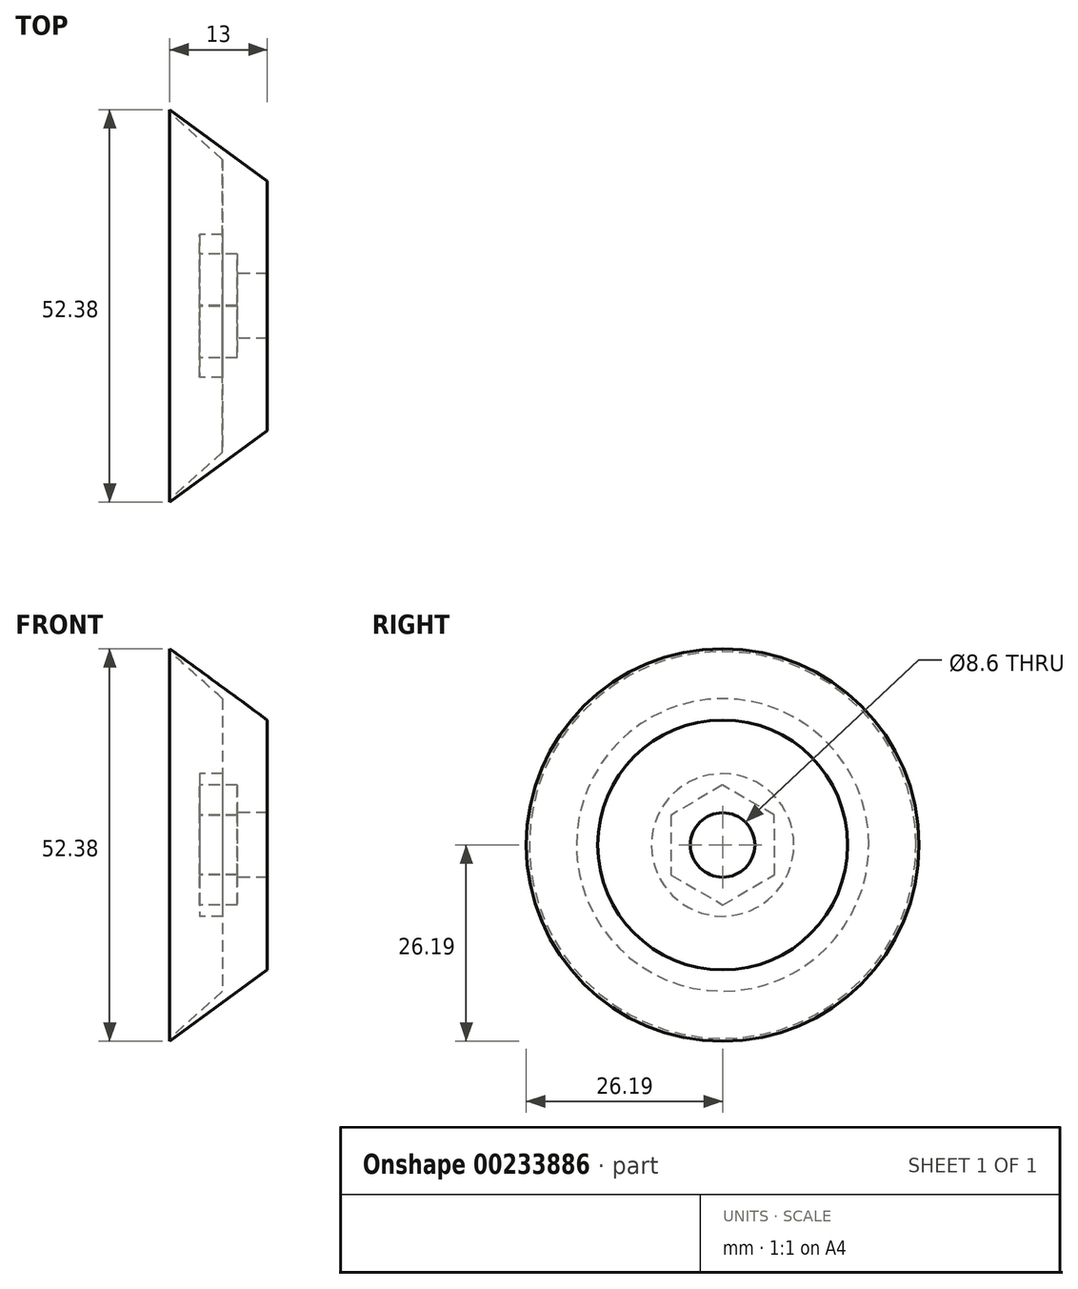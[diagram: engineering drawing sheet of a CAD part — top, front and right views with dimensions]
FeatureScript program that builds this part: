
annotation { "Feature Type Name" : "Feature", "Feature Type Description" : "" }
export const myFeature = defineFeature(function(context is Context, id is Id, definition is map)
    precondition{}
    {
        {
            var Q0;
            Q0=qCreatedBy(makeId("Front.planeOp"),FACE);
            var sketch = newSketch(context, id + "F0", { "sketchPlane" : qUnion([Q0])});
            skLineSegment(sketch, "E0", {"start": v(0, 72.01) * mm, "end": v(0, -72.04) * mm, "construction": true});
            skLineSegment(sketch, "E1", {"start": v(8, 67.17) * mm, "end": v(8, -65.75) * mm, "construction": true});
            skLineSegment(sketch, "E2", {"start": v(13, 61.84) * mm, "end": v(13, -59.21) * mm, "construction": true});
            skLineSegment(sketch, "E3", {"start": v(4, 59.18) * mm, "end": v(4, -52.92) * mm, "construction": true});
            skLineSegment(sketch, "E4", {"start": v(-49.7, 26.2) * mm, "end": v(61.22, 26.2) * mm, "construction": true});
            skLineSegment(sketch, "E5", {"start": v(-38.47, 14) * mm, "end": v(53.28, 14) * mm, "construction": true});
            skLineSegment(sketch, "E6", {"start": v(-32.84, 9.5) * mm, "end": v(36.11, 9.5) * mm, "construction": true});
            skLineSegment(sketch, "E7", {"start": v(-26.09, 4.3) * mm, "end": v(34.85, 4.3) * mm, "construction": true});
            skLineSegment(sketch, "E8", {"start": v(4, 4.3) * mm, "end": v(13, 4.3) * mm});
            skLineSegment(sketch, "E9", {"start": v(13, 4.3) * mm, "end": v(13, 9.5) * mm});
            skLineSegment(sketch, "E10", {"start": v(8, 14) * mm, "end": v(8, 19.5) * mm});
            skLineSegment(sketch, "E11", {"start": v(0, 26.2) * mm, "end": v(0, 25.79) * mm});
            skLineSegment(sketch, "E12", {"start": v(0, 25.79) * mm, "end": v(7.05, 19.5) * mm});
            skLineSegment(sketch, "E13", {"start": v(7.05, 19.5) * mm, "end": v(7.05, 9.5) * mm});
            skLineSegment(sketch, "E14", {"start": v(7.05, 9.5) * mm, "end": v(4, 9.5) * mm});
            skLineSegment(sketch, "E15", {"start": v(4, 9.5) * mm, "end": v(4, 4.3) * mm});
            skLineSegment(sketch, "E16", {"start": v(-60.7, 0) * mm, "end": v(65.05, 0) * mm, "construction": true});
            skLineSegment(sketch, "E17", {"start": v(0, 26.2) * mm, "end": v(13, 16.66) * mm});
            skLineSegment(sketch, "E18", {"start": v(13, 16.66) * mm, "end": v(13, 4.3) * mm});
            skSolve(sketch);
        }
        {
            var Q0;
            Q0=makeQuery(id+"F0.imprint","IMPRINT",FACE,{"disambiguationData":[TD([[makeQuery(id+"F0.imprint","IMPRINT",EDGE,{"derivedFrom":sQuery(id+"F0.wireOp",EDGE,"E8")}),1.0]])]});
            var Q1;
            Q1=sQuery(id+"F0.wireOp",EDGE,"E16");
            revolve(context, id + "F1", {"entities" : qUnion([Q0]), "axis" : qUnion([Q1]), "revolveType" : RevolveType.FULL});
        }
        {
            var Q0;
            Q0=makeQuery(id+"F1.opRevolve","SWEPT_FACE",FACE,{"disambiguationData":[OSD([sQuery(id+"F0.wireOp",EDGE,"E15")])]});
            var sketch = newSketch(context, id + "F2", { "sketchPlane" : qUnion([Q0])});
            skCircle(sketch, "E19.cCircle", {"center": v(0, 0) * mm, "radius": 6.91 * mm, "construction": true});
            skLineSegment(sketch, "E19.0", {"start": v(-6.9, 4.03) * mm, "end": v(0.04, 7.98) * mm});
            skLineSegment(sketch, "E19.1", {"start": v(0.04, 7.98) * mm, "end": v(6.93, 3.96) * mm});
            skLineSegment(sketch, "E19.2", {"start": v(6.93, 3.96) * mm, "end": v(6.9, -4.03) * mm});
            skLineSegment(sketch, "E19.3", {"start": v(6.9, -4.03) * mm, "end": v(-0.04, -7.98) * mm});
            skLineSegment(sketch, "E19.4", {"start": v(-0.04, -7.98) * mm, "end": v(-6.93, -3.96) * mm});
            skLineSegment(sketch, "E19.5", {"start": v(-6.93, -3.96) * mm, "end": v(-6.9, 4.03) * mm});
            skPoint(sketch, "E19.0.midPoint", {"position": v(-3.43, 6) * mm});
            skSolve(sketch);
        }
        {
            var Q0;
            Q0=makeQuery(id+"F2.imprint","IMPRINT",FACE,{"disambiguationData":[TD([[makeQuery(id+"F2.imprint","IMPRINT",EDGE,{"derivedFrom":sQuery(id+"F2.wireOp",EDGE,"E19.0")}),-1.0]])]});
            extrude(context, id + "F3", {"entities" : qUnion([Q0]), "operationType" : NewBodyOperationType.REMOVE, "oppositeDirection" : true, "depth" : 5 * mm});
        }
    });
